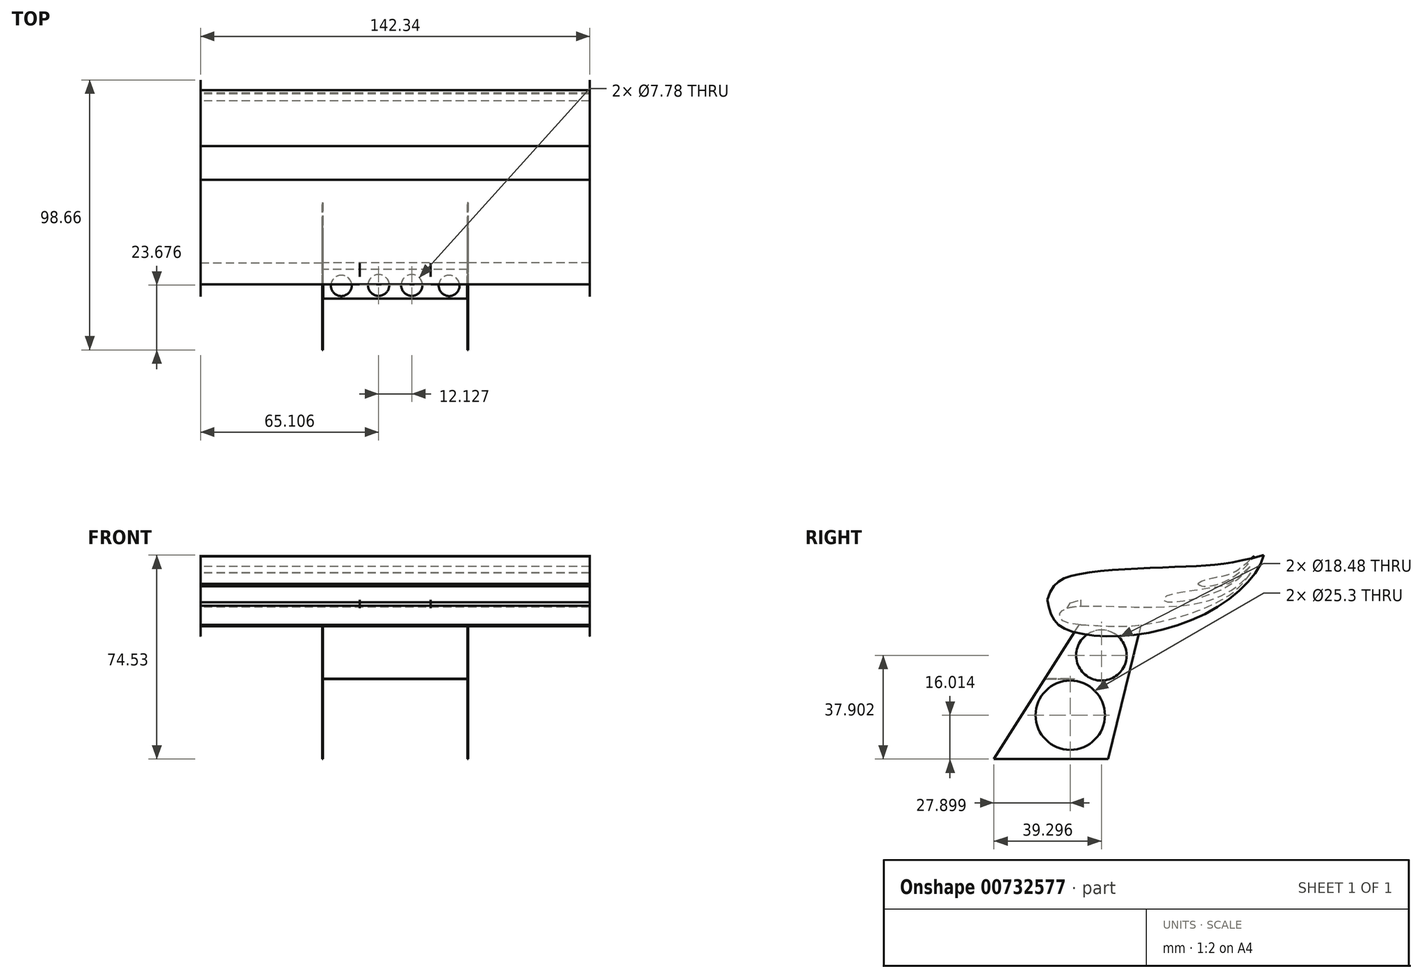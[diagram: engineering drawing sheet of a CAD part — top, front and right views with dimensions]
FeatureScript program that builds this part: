
annotation { "Feature Type Name" : "Feature", "Feature Type Description" : "" }
export const myFeature = defineFeature(function(context is Context, id is Id, definition is map)
    precondition{}
    {
        {
            var Q0;
            Q0=qCreatedBy(makeId("Right.planeOp"),FACE);
            var sketch = newSketch(context, id + "F0", { "sketchPlane" : qUnion([Q0])});
            skFitSpline(sketch, "E0", {"points": [v(-42.15, 19.82) * mm, v(-22.33, 19.52) * mm, v(4.3, 26.42) * mm, v(16.87, 34.75) * mm, v(19.97, 38.82) * mm], "startDerivative": vector(65.1, -2.26) * mm, "endDerivative": vector(2.68, 4.63) * mm});
            skFitSpline(sketch, "E1", {"points": [v(-42.15, 19.82) * mm, v(-49.84, 23.96) * mm, v(-42.15, 26.62) * mm, v(7.02, 29.43) * mm, v(19.97, 38.82) * mm], "startDerivative": vector(-122.44, 0.98) * mm, "endDerivative": vector(4.35, 6.9) * mm});
            skFitSpline(sketch, "E2", {"points": [v(19.58, 41.16) * mm, v(9.86, 32.88) * mm, v(-4.45, 28.48) * mm, v(-11.5, 28.4) * mm, v(-11.75, 29.5) * mm, v(-9.87, 30.78) * mm, v(6.16, 33.47) * mm, v(12.61, 35.4) * mm, v(17.1, 38.74) * mm], "startDerivative": vector(-36.13, -55.86) * mm, "endDerivative": vector(32.85, 32.82) * mm});
            skLineSegment(sketch, "E3", {"start": v(19.58, 41.16) * mm, "end": v(17.1, 38.74) * mm});
            skFitSpline(sketch, "E4", {"points": [v(0.55, 34.77) * mm, v(2.11, 34) * mm, v(8.93, 35) * mm, v(16.2, 39.38) * mm, v(20.96, 44.85) * mm], "startDerivative": vector(8.92, -7.13) * mm, "endDerivative": vector(14.83, 24.19) * mm});
            skFitSpline(sketch, "E5", {"points": [v(0.55, 34.77) * mm, v(2.11, 35.82) * mm, v(9.2, 37.55) * mm, v(15.5, 40.08) * mm, v(20.96, 44.88) * mm, v(20.96, 44.85) * mm], "startDerivative": vector(8.09, 7.18) * mm, "endDerivative": vector(-2.25, -8.9) * mm});
            skSolve(sketch);
        }
        {
            var Q0;
            Q0 = qSketchRegion(id + "F0", true);
            var Q1;
            {var subQ0=sQuery(id+"F0.wireOp",EDGE,"E1");var subQ1=sQuery(id+"F0.wireOp",EDGE,"E0");var subQ2=makeQuery(id+"F0.imprint","INTERSECT",VERTEX,{"disambiguationData":[OD(0.0)],"derivedFrom":[subQ1,subQ0]});Q1=makeQuery(id+"F0.imprint","IMPRINT",FACE,{"disambiguationData":[TD([[makeQuery(id+"F0.imprint","IMPRINT",EDGE,{"disambiguationData":[TD([[subQ2,-1.0]])],"derivedFrom":subQ1}),1.0]])]});}
            extrude(context, id + "F1", {"entities" : qUnion([Q0, Q1]), "depth" : 71.12 * mm, "offsetDistance" : 25.4 * mm});
        }
        {
            var Q0;
            Q0=qCreatedBy(makeId("Right.planeOp"),FACE);
            cPlane(context, id + "F2", {"entities" : qUnion([Q0]), "cplaneType" : CPlaneType.OFFSET, "offset" : 71.15 * mm, "width" : 152.4 * mm, "height" : 152.4 * mm});
        }
        {
            var Q0;
            Q0=qCreatedBy(id+"F2.planeOp",FACE);
            var sketch = newSketch(context, id + "F3", { "sketchPlane" : qUnion([Q0])});
            skFitSpline(sketch, "E6", {"points": [v(-54.44, 28.88) * mm, v(-48.38, 18.53) * mm, v(-6.82, 19.58) * mm, v(24.7, 45.26) * mm], "startDerivative": vector(12.9, -71.9) * mm, "endDerivative": vector(19.44, 76.25) * mm});
            skFitSpline(sketch, "E7", {"points": [v(-54.44, 28.88) * mm, v(-44.18, 38.04) * mm, v(-3.58, 41.09) * mm, v(24.7, 45.26) * mm], "startDerivative": vector(20.94, 74.77) * mm, "endDerivative": vector(100.98, 27.17) * mm});
            skSolve(sketch);
        }
        {
            var Q0;
            Q0=makeQuery(id+"F3.imprint","IMPRINT",FACE,{"disambiguationData":[TD([[makeQuery(id+"F3.imprint","IMPRINT",EDGE,{"derivedFrom":sQuery(id+"F3.wireOp",EDGE,"E6")}),1.0]])]});
            extrude(context, id + "F4", {"entities" : qUnion([Q0]), "depth" : 0.03 * mm, "offsetDistance" : 25.4 * mm});
        }
        {
            var Q0;
            Q0=qCreatedBy(makeId("Right.planeOp"),FACE);
            cPlane(context, id + "F5", {"entities" : qUnion([Q0]), "cplaneType" : CPlaneType.OFFSET, "offset" : 12.95 * mm, "width" : 152.4 * mm, "height" : 152.4 * mm});
        }
        {
            var Q0;
            Q0=qCreatedBy(id+"F5.planeOp",FACE);
            var sketch = newSketch(context, id + "F6", { "sketchPlane" : qUnion([Q0])});
            skLineSegment(sketch, "E8", {"start": v(-43.73, 25.51) * mm, "end": v(-48.32, 23.98) * mm});
            skLineSegment(sketch, "E9", {"start": v(-48.32, 23.98) * mm, "end": v(-46.03, 27.72) * mm});
            skPoint(sketch, "E9.endSnap0", {"position": v(-46.03, 24.75) * mm});
            skLineSegment(sketch, "E10", {"start": v(-46.03, 27.72) * mm, "end": v(-42.28, 28.97) * mm});
            skLineSegment(sketch, "E11", {"start": v(-42.28, 28.97) * mm, "end": v(-42.28, 25.51) * mm});
            skLineSegment(sketch, "E12", {"start": v(-42.28, 25.51) * mm, "end": v(-43.73, 25.51) * mm});
            skSolve(sketch);
        }
        {
            var Q0;
            Q0=makeQuery(id+"F6.imprint","IMPRINT",FACE,{"disambiguationData":[TD([[makeQuery(id+"F6.imprint","IMPRINT",EDGE,{"derivedFrom":sQuery(id+"F6.wireOp",EDGE,"E8")}),-1.0]])]});
            extrude(context, id + "F7", {"entities" : qUnion([Q0]), "operationType" : NewBodyOperationType.ADD, "depth" : 0 * mm, "offsetDistance" : 25.4 * mm});
        }
        {
            var Q0;
            Q0=qCreatedBy(id+"F5.planeOp",FACE);
            cPlane(context, id + "F8", {"entities" : qUnion([Q0]), "cplaneType" : CPlaneType.OFFSET, "offset" : 13.46 * mm, "width" : 152.4 * mm, "height" : 152.4 * mm});
        }
        {
            var Q0;
            Q0=qCreatedBy(id+"F8.planeOp",FACE);
            var sketch = newSketch(context, id + "F9", { "sketchPlane" : qUnion([Q0])});
            skLineSegment(sketch, "E13", {"start": v(-19.31, 23.32) * mm, "end": v(-32.25, -29.27) * mm});
            skLineSegment(sketch, "E14", {"start": v(-32.25, -29.27) * mm, "end": v(-73.96, -29.27) * mm});
            skLineSegment(sketch, "E15", {"start": v(-73.96, -29.27) * mm, "end": v(-41.85, 21.3) * mm});
            skLineSegment(sketch, "E16", {"start": v(-41.85, 21.3) * mm, "end": v(-19.31, 23.32) * mm});
            skCircle(sketch, "E17", {"center": v(-34.66, 8.63) * mm, "radius": 9.24 * mm});
            skCircle(sketch, "E18", {"center": v(-46.06, -13.26) * mm, "radius": 12.65 * mm});
            skSolve(sketch);
        }
        {
            var Q0;
            Q0 = qSketchRegion(id + "F9", true);
            extrude(context, id + "F10", {"entities" : qUnion([Q0]), "operationType" : NewBodyOperationType.ADD, "depth" : 0.25 * mm, "offsetDistance" : 25.4 * mm});
        }
        {
            var Q0;
            Q0=qCreatedBy(makeId("Top.planeOp"),FACE);
            var sketch = newSketch(context, id + "F11", { "sketchPlane" : qUnion([Q0])});
            skLineSegment(sketch, "E19", {"start": v(26.3, -55.2) * mm, "end": v(26.3, -44.52) * mm});
            skLineSegment(sketch, "E20", {"start": v(26.3, -55.2) * mm, "end": v(0, -55.2) * mm});
            skLineSegment(sketch, "E21", {"start": v(26.3, -44.52) * mm, "end": v(0, -44.52) * mm});
            skLineSegment(sketch, "E22", {"start": v(0, -44.52) * mm, "end": v(0, -55.2) * mm});
            skCircle(sketch, "E23", {"center": v(6.06, -50.28) * mm, "radius": 3.9 * mm});
            skCircle(sketch, "E24", {"center": v(19.7, -50.46) * mm, "radius": 3.8 * mm});
            skSolve(sketch);
        }
        {
            var Q0;
            Q0 = qSketchRegion(id + "F11", true);
            var Q1;
            Q1=makeQuery(id+"F11.imprint","IMPRINT",FACE,{"disambiguationData":[TD([[makeQuery(id+"F11.imprint","IMPRINT",EDGE,{"derivedFrom":sQuery(id+"F11.wireOp",EDGE,"E19")}),1.0]])]});
            extrude(context, id + "F12", {"entities" : qUnion([Q0, Q1]), "depth" : 0.03 * mm, "offsetDistance" : 25.4 * mm});
        }
        {
            var Q0;
            {var subQ0=sQuery(id+"F0.wireOp",EDGE,"E1");var subQ1=sQuery(id+"F0.wireOp",EDGE,"E0");var subQ2=makeQuery(id+"F0.imprint","INTERSECT",VERTEX,{"disambiguationData":[OD(0.0)],"derivedFrom":[subQ1,subQ0]});Q0=makeQuery(id+"F1.opExtrude","SWEPT_BODY",BODY,{"disambiguationData":[OSD([subQ1,subQ0]),TDD([makeQuery(id+"F0.imprint","IMPRINT",EDGE,{"disambiguationData":[TD([[subQ2,-1.0]])],"derivedFrom":subQ1}),makeQuery(id+"F0.imprint","IMPRINT",EDGE,{"disambiguationData":[TD([[subQ2,-1.0]])],"derivedFrom":subQ0})])]});}
            var Q1;
            {var subQ0=sQuery(id+"F0.wireOp",EDGE,"E1");var subQ1=sQuery(id+"F0.wireOp",EDGE,"E0");var subQ2=makeQuery(id+"F0.imprint","INTERSECT",VERTEX,{"disambiguationData":[OD(1.0)],"derivedFrom":[subQ1,subQ0]});Q1=makeQuery(id+"F1.opExtrude","SWEPT_BODY",BODY,{"disambiguationData":[OSD([subQ1,subQ0]),TDD([makeQuery(id+"F0.imprint","IMPRINT",EDGE,{"disambiguationData":[TD([[subQ2,1.0]])],"derivedFrom":subQ1}),makeQuery(id+"F0.imprint","IMPRINT",EDGE,{"disambiguationData":[TD([[subQ2,1.0]])],"derivedFrom":subQ0})])]});}
            var Q2;
            Q2=makeQuery(id+"F4.opExtrude","SWEPT_BODY",BODY,{"disambiguationData":[OSD([sQuery(id+"F3.wireOp",EDGE,"E6"),sQuery(id+"F3.wireOp",EDGE,"E7")])]});
            var Q3;
            Q3=makeQuery(id+"F12.opExtrude","SWEPT_BODY",BODY,{"disambiguationData":[OSD([sQuery(id+"F11.wireOp",EDGE,"E19"),sQuery(id+"F11.wireOp",EDGE,"E20"),sQuery(id+"F11.wireOp",EDGE,"E21"),sQuery(id+"F11.wireOp",EDGE,"E22"),sQuery(id+"F11.wireOp",EDGE,"E23"),sQuery(id+"F11.wireOp",EDGE,"E24")])]});
            var Q4;
            Q4=makeQuery(id+"F1.opExtrude","SWEPT_BODY",BODY,{"disambiguationData":[OSD([sQuery(id+"F0.wireOp",EDGE,"E2"),sQuery(id+"F0.wireOp",EDGE,"E3")])]});
            var Q5;
            Q5=makeQuery(id+"F1.opExtrude","SWEPT_BODY",BODY,{"disambiguationData":[OSD([sQuery(id+"F0.wireOp",EDGE,"E4"),sQuery(id+"F0.wireOp",EDGE,"E5")])]});
            var Q6;
            Q6=qCreatedBy(makeId("Right.planeOp"),FACE);
            mirror(context, id + "F13", {"operationType" : NewBodyOperationType.ADD, "entities" : qUnion([Q0, Q1, Q2, Q3, Q4, Q5]), "mirrorPlane" : qUnion([Q6])});
        }
    });
